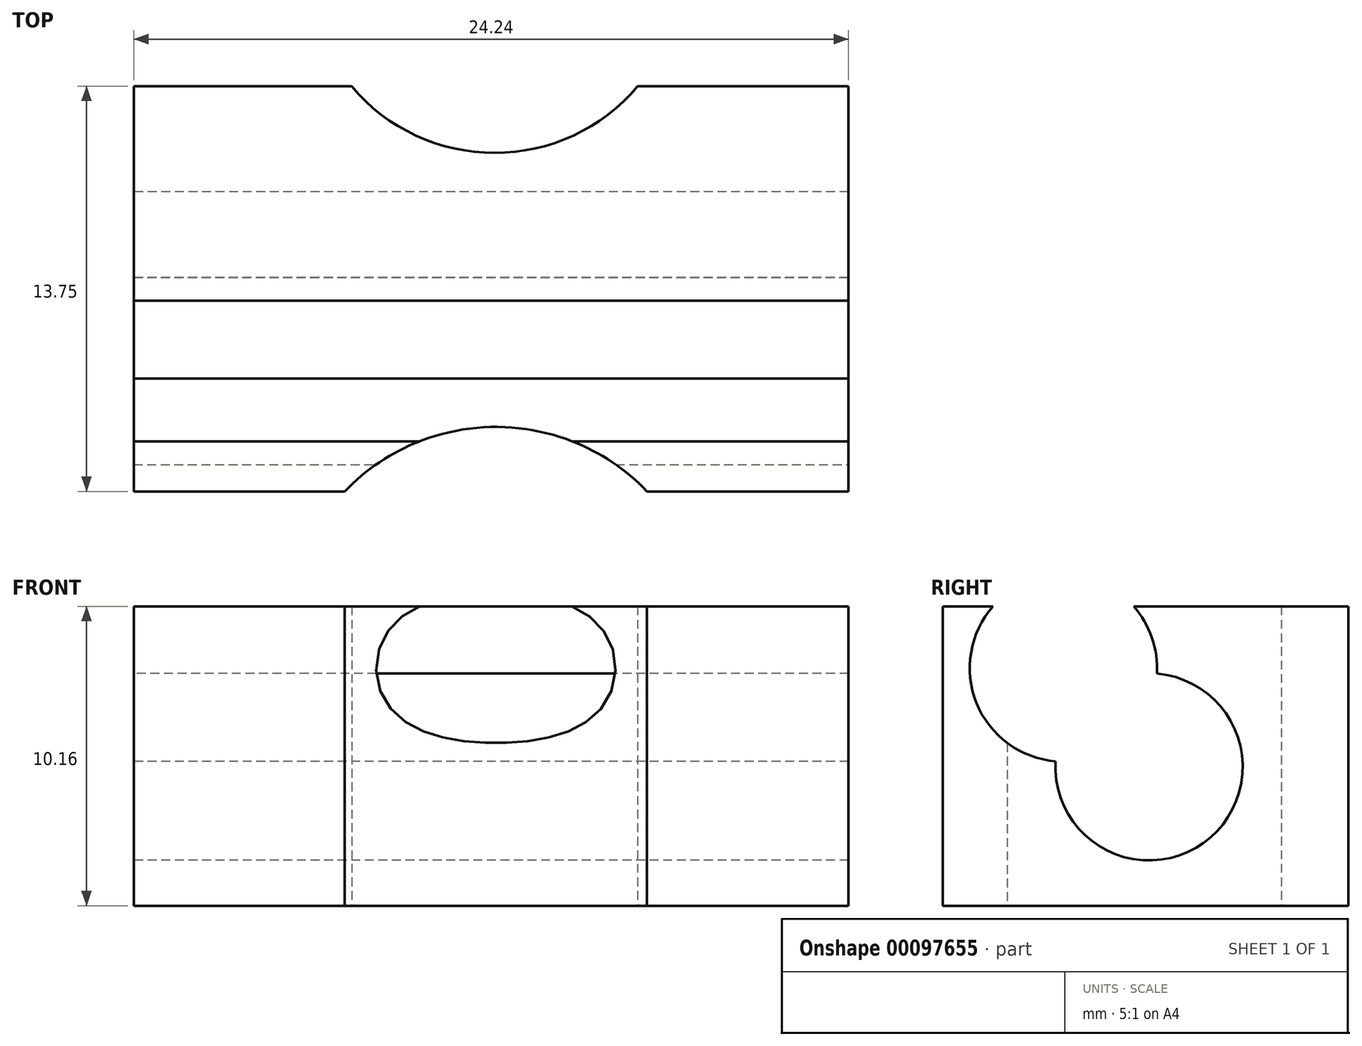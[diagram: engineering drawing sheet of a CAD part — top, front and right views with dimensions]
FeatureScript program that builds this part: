
annotation { "Feature Type Name" : "Feature", "Feature Type Description" : "" }
export const myFeature = defineFeature(function(context is Context, id is Id, definition is map)
    precondition{}
    {
        {
            var Q0;
            Q0=qCreatedBy(makeId("Top.planeOp"),FACE);
            var sketch = newSketch(context, id + "F0", { "sketchPlane" : qUnion([Q0])});
            skLineSegment(sketch, "E0.bottom", {"start": v(0, 0) * mm, "end": v(7.16, 0) * mm});
            skLineSegment(sketch, "E0.top", {"start": v(0, 13.75) * mm, "end": v(7.4, 13.75) * mm});
            skLineSegment(sketch, "E0.left", {"start": v(0, 0) * mm, "end": v(0, 13.75) * mm});
            skLineSegment(sketch, "E0.right", {"start": v(24.24, 0) * mm, "end": v(24.24, 13.75) * mm});
            skArc(sketch, "E1", {"start": v(17.41, 0) * mm, "mid": v(12.28, 2.19) * mm, "end": v(7.16, 0) * mm});
            skArc(sketch, "E2.MirrorCS", {"start": v(17.1, 13.75) * mm, "mid": v(12.24, 11.48) * mm, "end": v(7.4, 13.75) * mm});
            skLineSegment(sketch, "E3.trimOffspring", {"start": v(17.1, 13.75) * mm, "end": v(24.24, 13.75) * mm});
            skLineSegment(sketch, "E4.trimOffspring", {"start": v(17.41, 0) * mm, "end": v(24.24, 0) * mm});
            skSolve(sketch);
        }
        {
            var Q0;
            Q0=makeQuery(id+"F0.imprint","IMPRINT",FACE,{"disambiguationData":[TD([[makeQuery(id+"F0.imprint","IMPRINT",EDGE,{"derivedFrom":sQuery(id+"F0.wireOp",EDGE,"E0.bottom")}),1.0]])]});
            extrude(context, id + "F1", {"entities" : qUnion([Q0]), "depth" : 10.16 * mm});
        }
        {
            var Q0;
            Q0=makeQuery(id+"F1.opExtrude","SWEPT_FACE",FACE,{"disambiguationData":[OSD([sQuery(id+"F0.wireOp",EDGE,"E0.left")])]});
            var sketch = newSketch(context, id + "F2", { "sketchPlane" : qUnion([Q0])});
            skCircle(sketch, "E5", {"center": v(-7, 4.71) * mm, "radius": 3.17 * mm});
            skSolve(sketch);
        }
        {
            var Q0;
            Q0=makeQuery(id+"F1.opExtrude","SWEPT_FACE",FACE,{"disambiguationData":[OSD([sQuery(id+"F0.wireOp",EDGE,"E0.right")])]});
            var sketch = newSketch(context, id + "F3", { "sketchPlane" : qUnion([Q0])});
            skCircle(sketch, "E6", {"center": v(4.09, 8.06) * mm, "radius": 2.04 * mm});
            skSolve(sketch);
        }
        {
            var Q0;
            Q0=sQuery(id+"F3.wireOp",VERTEX,"E6.center");
            var Q1;
            Q1=sQuery(id+"F2.wireOp",VERTEX,"E5.center");
            var Q2;
            Q2=makeQuery(id+"F1.opExtrude","SWEPT_BODY",BODY,{"disambiguationData":[OSD([sQuery(id+"F0.wireOp",EDGE,"E0.bottom"),sQuery(id+"F0.wireOp",EDGE,"E0.top"),sQuery(id+"F0.wireOp",EDGE,"E0.left"),sQuery(id+"F0.wireOp",EDGE,"E0.right"),sQuery(id+"F0.wireOp",EDGE,"E1"),sQuery(id+"F0.wireOp",EDGE,"E2.MirrorCS"),sQuery(id+"F0.wireOp",EDGE,"E3.trimOffspring"),sQuery(id+"F0.wireOp",EDGE,"E4.trimOffspring")])]});
            hole(context, id + "F4", {"style" : HoleStyle.SIMPLE, "endStyle" : HoleEndStyle.THROUGH, "holeDiameter" : 6.35 * mm, "locations" : qUnion([Q0, Q1]), "scope" : qUnion([Q2]), "isTappedThrough" : true});
        }
    });
